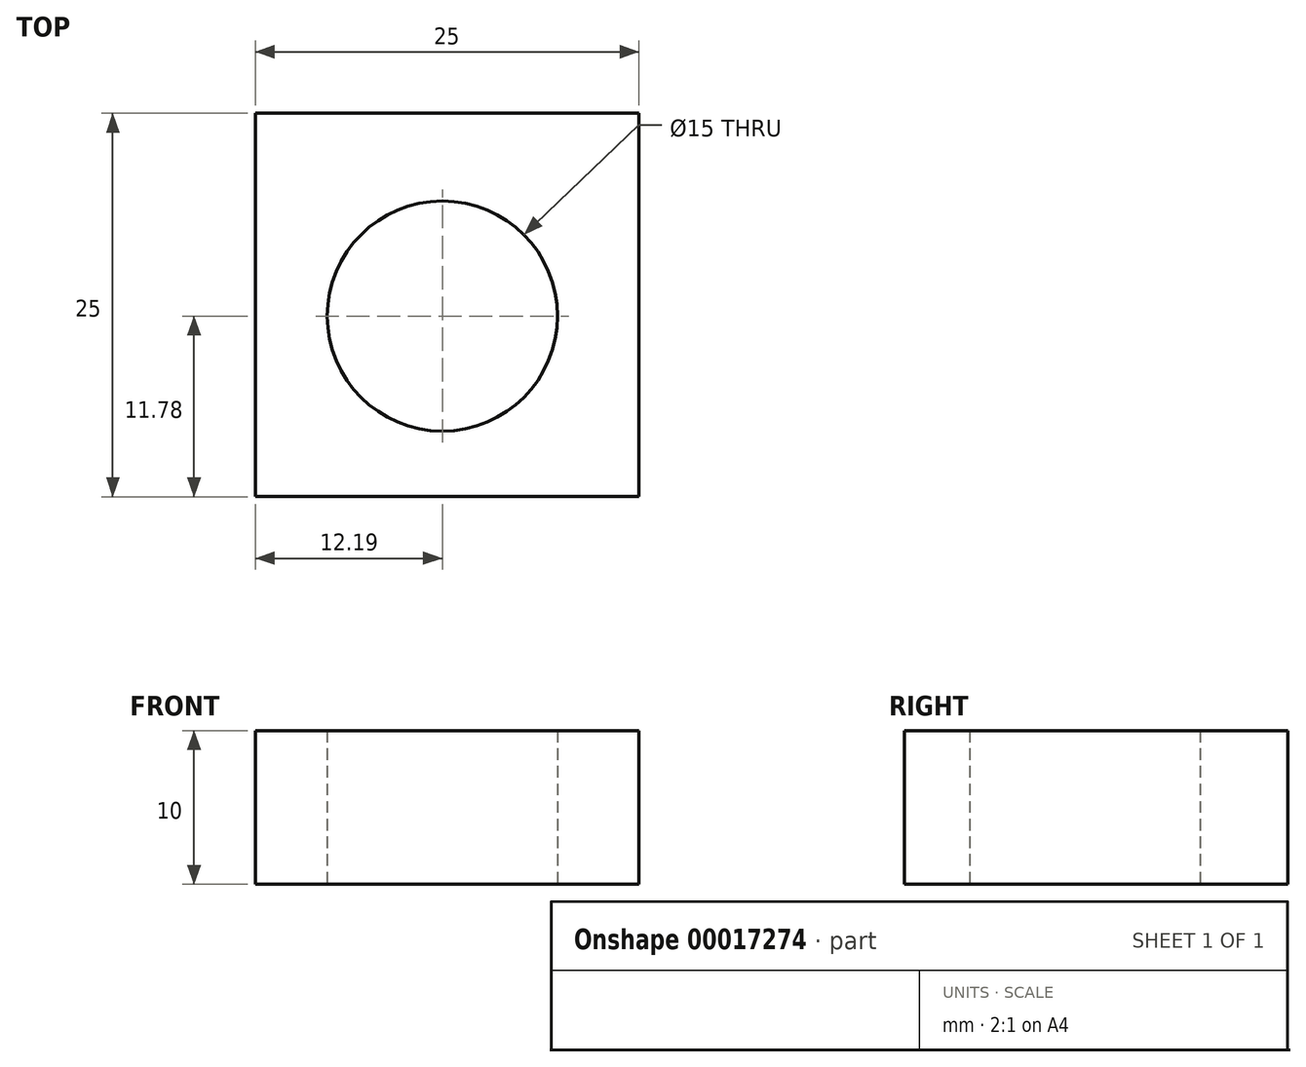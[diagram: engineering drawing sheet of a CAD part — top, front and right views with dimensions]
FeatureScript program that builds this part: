
annotation { "Feature Type Name" : "Feature", "Feature Type Description" : "" }
export const myFeature = defineFeature(function(context is Context, id is Id, definition is map)
    precondition{}
    {
        {
            var Q0;
            Q0=qCreatedBy(makeId("Top.planeOp"),FACE);
            var sketch = newSketch(context, id + "F0", { "sketchPlane" : qUnion([Q0])});
            skLineSegment(sketch, "E0.bottom", {"start": v(-12.2, 13.22) * mm, "end": v(12.8, 13.22) * mm});
            skLineSegment(sketch, "E0.top", {"start": v(-12.2, -11.78) * mm, "end": v(12.8, -11.78) * mm});
            skLineSegment(sketch, "E0.left", {"start": v(-12.2, 13.22) * mm, "end": v(-12.2, -11.78) * mm});
            skLineSegment(sketch, "E0.right", {"start": v(12.8, 13.22) * mm, "end": v(12.8, -11.78) * mm});
            skCircle(sketch, "E1", {"center": v(0, 0) * mm, "radius": 7.5 * mm});
            skSolve(sketch);
        }
        {
            var Q0;
            Q0 = qSketchRegion(id + "F0", true);
            extrude(context, id + "F1", {"entities" : qUnion([Q0]), "depth" : 10 * mm});
        }
    });
